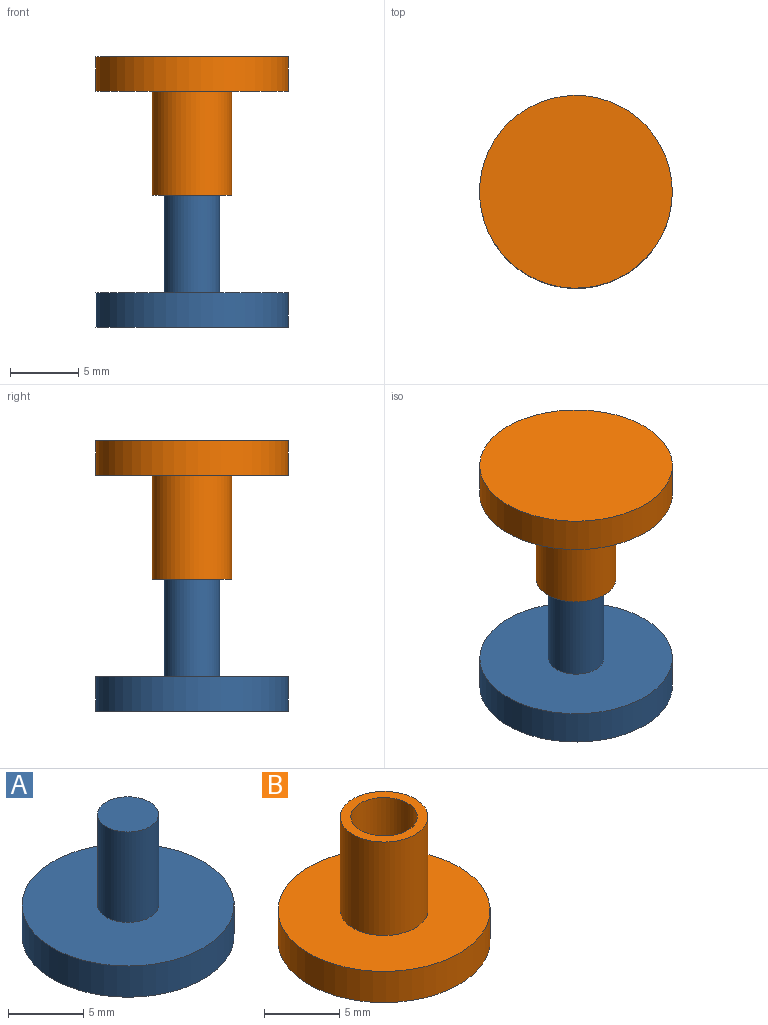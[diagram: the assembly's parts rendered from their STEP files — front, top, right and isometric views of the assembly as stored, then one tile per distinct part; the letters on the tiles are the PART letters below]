
ASSEMBLY  parts=2 mates=1
PART A: 5 faces, bbox 14.1x14.1x9.9 mm
  f0: cylinder r=7.06mm len=14.11mm, axis (0,0,1), area 112.6mm2, adj f1,f2
  f1: plane 14.11x14.11mm, normal (0,0,-1), area 156.4mm2, adj f0
  f2: plane 14.11x14.11mm, normal (0,0,1), area 143.4mm2, adj f0,f3
  f3: cylinder r=2.03mm len=7.37mm, axis (0,0,-1), area 94mm2, adj f2,f4
  f4: plane 4.06x4.06mm, normal (0,0,1), area 13mm2, adj f3
PART B: 7 faces, bbox 14.1x14.1x10.2 mm
  f0: cylinder r=7.06mm len=14.12mm, axis (0,0,-1), area 112.7mm2, adj f1,f2
  f1: plane 14.12x14.12mm, normal (0,0,1), area 129.8mm2, adj f0,f4
  f2: plane 14.12x14.12mm, normal (0,0,-1), area 156.6mm2, adj f0
  f3: cylinder r=2.21mm len=7.62mm, axis (0,0,-1), area 105.9mm2, adj f5,f6
  f4: cylinder r=2.92mm len=7.62mm, axis (0,0,-1), area 139.9mm2, adj f1,f5
  f5: plane 5.84x5.84mm, normal (0,0,1), area 11.4mm2, adj f3,f4
  f6: plane 4.42x4.42mm, normal (0,0,1), area 15.4mm2, adj f3
PLACE A t=(-3.91,-2.61,-2.67)mm
PLACE B rot(axis=(-1,0,0),180deg) t=(-3.91,-2.61,14.6)mm
MATE slider A.f3 <-> B.f3  axis (0,0,-1) through (-3.91,-2.61,4.7)mm
